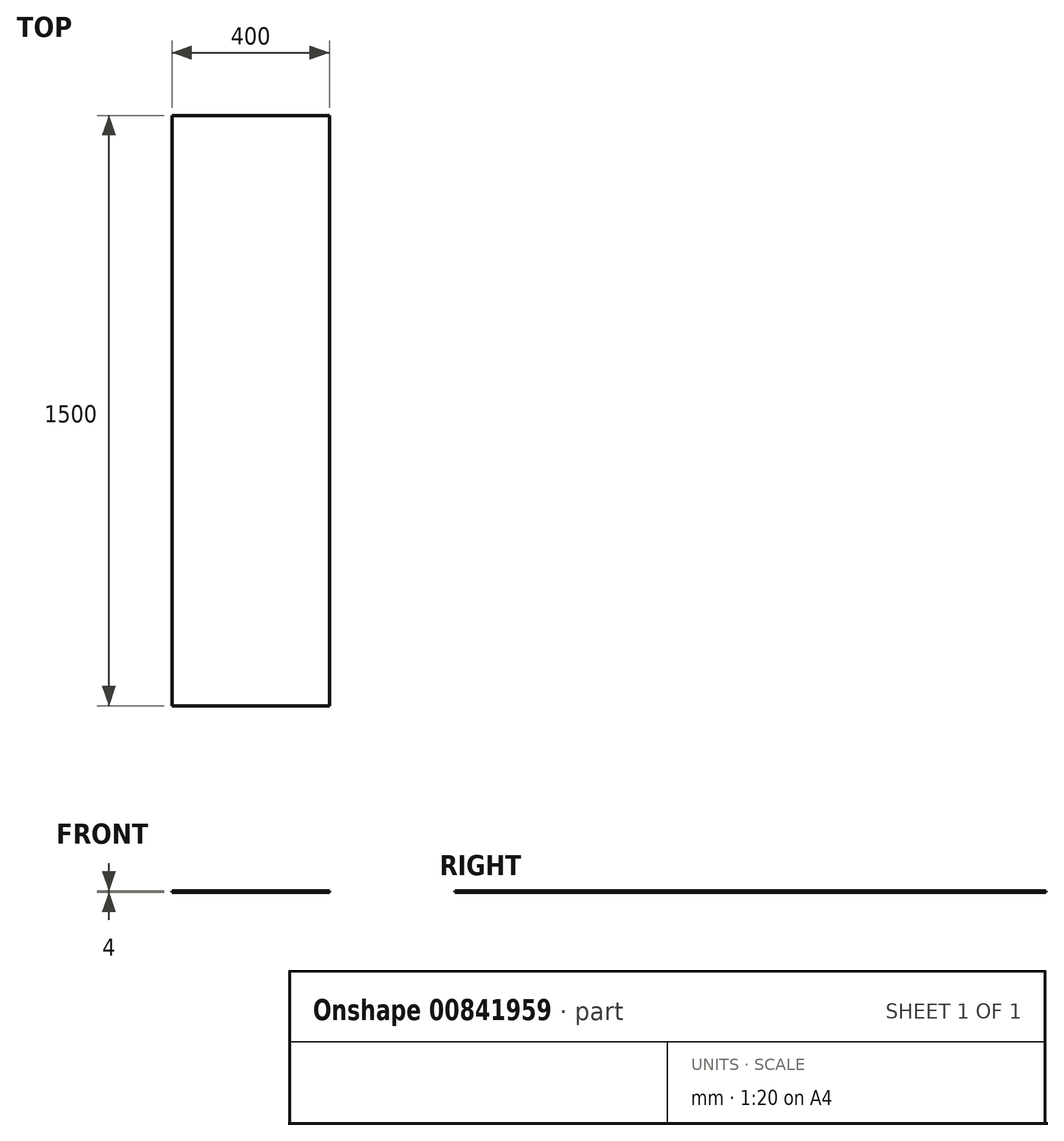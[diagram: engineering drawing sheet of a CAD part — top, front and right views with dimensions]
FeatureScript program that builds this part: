
annotation { "Feature Type Name" : "Feature", "Feature Type Description" : "" }
export const myFeature = defineFeature(function(context is Context, id is Id, definition is map)
    precondition{}
    {
        {
            var Q0;
            Q0=qCreatedBy(makeId("Front.planeOp"),FACE);
            var sketch = newSketch(context, id + "F0", { "sketchPlane" : qUnion([Q0])});
            skLineSegment(sketch, "E0.bottom", {"start": v(-200, 2) * mm, "end": v(200, 2) * mm});
            skLineSegment(sketch, "E0.top", {"start": v(-200, -2) * mm, "end": v(200, -2) * mm});
            skLineSegment(sketch, "E0.left", {"start": v(-200, 2) * mm, "end": v(-200, -2) * mm});
            skLineSegment(sketch, "E0.right", {"start": v(200, 2) * mm, "end": v(200, -2) * mm});
            skSolve(sketch);
        }
        {
            var Q0;
            Q0=makeQuery(id+"F0.imprint","IMPRINT",FACE,{"disambiguationData":[TD([[makeQuery(id+"F0.imprint","IMPRINT",EDGE,{"derivedFrom":sQuery(id+"F0.wireOp",EDGE,"E0.bottom")}),-1.0]])]});
            extrude(context, id + "F1", {"entities" : qUnion([Q0]), "endBound" : BoundingType.SYMMETRIC, "depth" : 1500 * mm, "offsetDistance" : 25 * mm});
        }
    });
